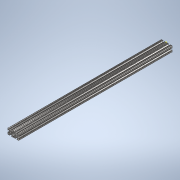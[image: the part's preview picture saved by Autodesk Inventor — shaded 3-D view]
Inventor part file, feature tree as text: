
AUTODESK INVENTOR PART (.ipt)
format: ipt  version: 2020 (Build 240168000, 168)  size: 357,376 bytes
history: native  units: in
note: dims shown in document units (in); Inventor stores cm internally (conversion verified against a paired STEP export)
features: sketch x2, extrude x1
ambient origin geometry x8: Origin, YZ Plane, XZ Plane, XY Plane, X Axis, Y Axis, Z Axis, Center Point
bodies: Solid1 (feature_tree)
feature tree (3):
  extrude  "Extrusion1"  [1 undecoded]
  sketch  "Sketch2"
  sketch  "Sketch1"  dims[d0=27.0in d1=0.0in]
note: 1 required parameter value undecoded (feature->parameter linkage not recoverable at this tier; creation-order binding heuristic only, values carry confidence <= 0.55)
